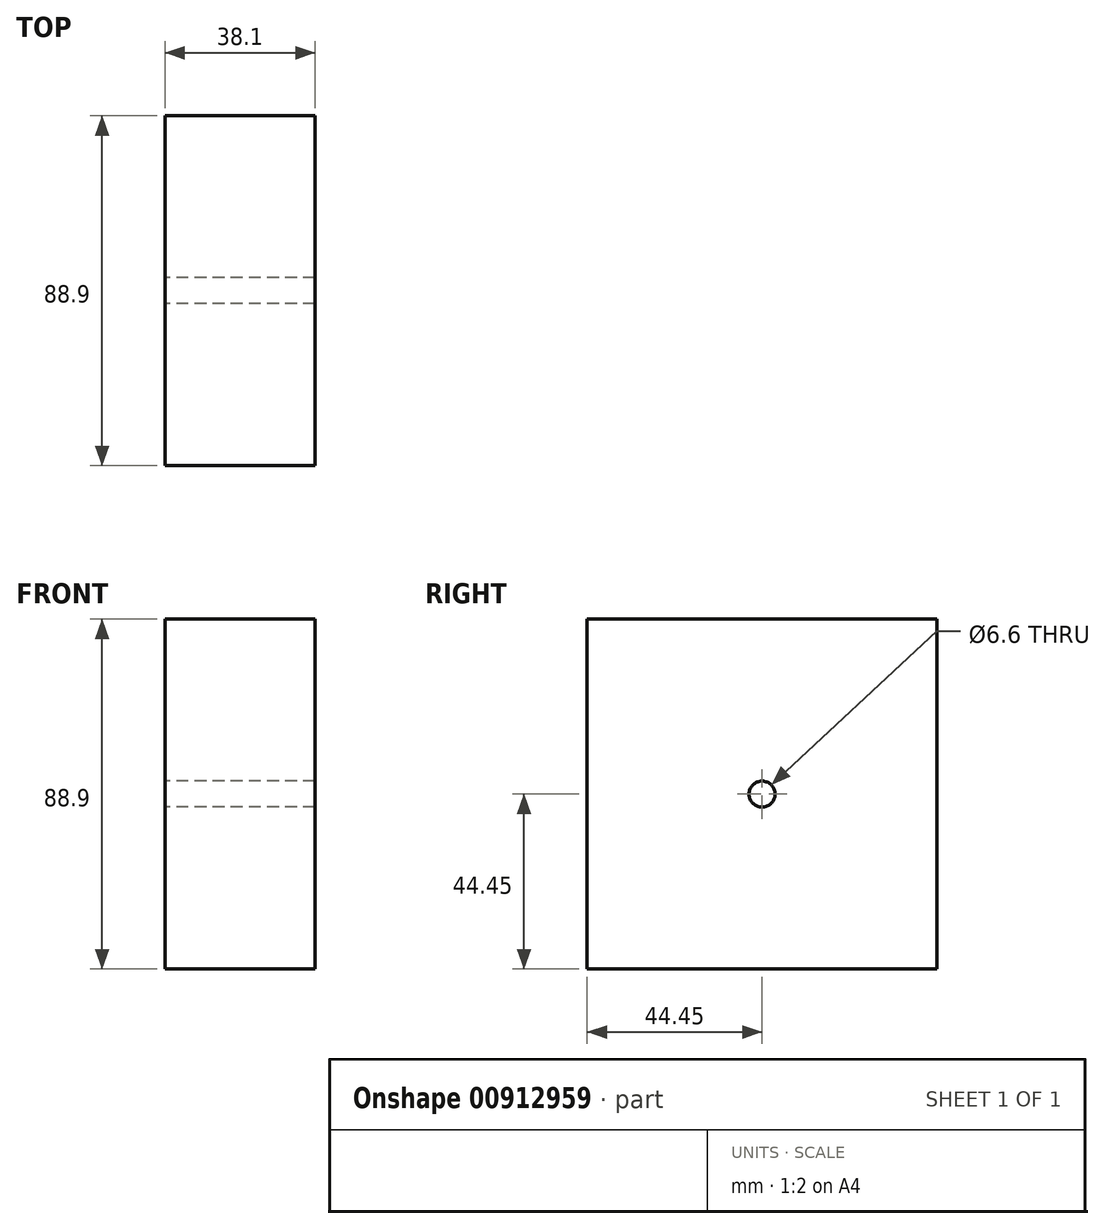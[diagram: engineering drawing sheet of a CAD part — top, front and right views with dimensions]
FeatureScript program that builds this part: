
annotation { "Feature Type Name" : "Feature", "Feature Type Description" : "" }
export const myFeature = defineFeature(function(context is Context, id is Id, definition is map)
    precondition{}
    {
        {
            var Q0;
            Q0=qCreatedBy(makeId("Front.planeOp"),FACE);
            var sketch = newSketch(context, id + "F0", { "sketchPlane" : qUnion([Q0])});
            skLineSegment(sketch, "E0.bottom", {"start": v(19.05, 44.45) * mm, "end": v(-19.05, 44.45) * mm});
            skLineSegment(sketch, "E0.top", {"start": v(19.05, -44.45) * mm, "end": v(-19.05, -44.45) * mm});
            skLineSegment(sketch, "E0.left", {"start": v(19.05, 44.45) * mm, "end": v(19.05, -44.45) * mm});
            skLineSegment(sketch, "E0.right", {"start": v(-19.05, 44.45) * mm, "end": v(-19.05, -44.45) * mm});
            skPoint(sketch, "E0.middle", {"position": v(0, 0) * mm});
            skSolve(sketch);
        }
        {
            var Q0;
            Q0 = qSketchRegion(id + "F0", true);
            extrude(context, id + "F1", {"entities" : qUnion([Q0]), "depth" : 88.9 * mm, "offsetDistance" : 25.4 * mm});
        }
        {
            var Q0;
            Q0=makeQuery(id+"F1.opExtrude","SWEPT_FACE",FACE,{"disambiguationData":[OSD([sQuery(id+"F0.wireOp",EDGE,"E0.right")])]});
            var sketch = newSketch(context, id + "F2", { "sketchPlane" : qUnion([Q0])});
            skLineSegment(sketch, "E1", {"start": v(0, -44.45) * mm, "end": v(88.9, 44.45) * mm, "construction": true});
            skCircle(sketch, "E2", {"center": v(44.45, 0) * mm, "radius": 3.3 * mm});
            skSolve(sketch);
        }
        {
            var Q0;
            Q0 = qSketchRegion(id + "F2", true);
            extrude(context, id + "F3", {"entities" : qUnion([Q0]), "operationType" : NewBodyOperationType.REMOVE, "endBound" : BoundingType.THROUGH_ALL, "oppositeDirection" : true, "depth" : 25.4 * mm, "offsetDistance" : 25.4 * mm});
        }
    });
